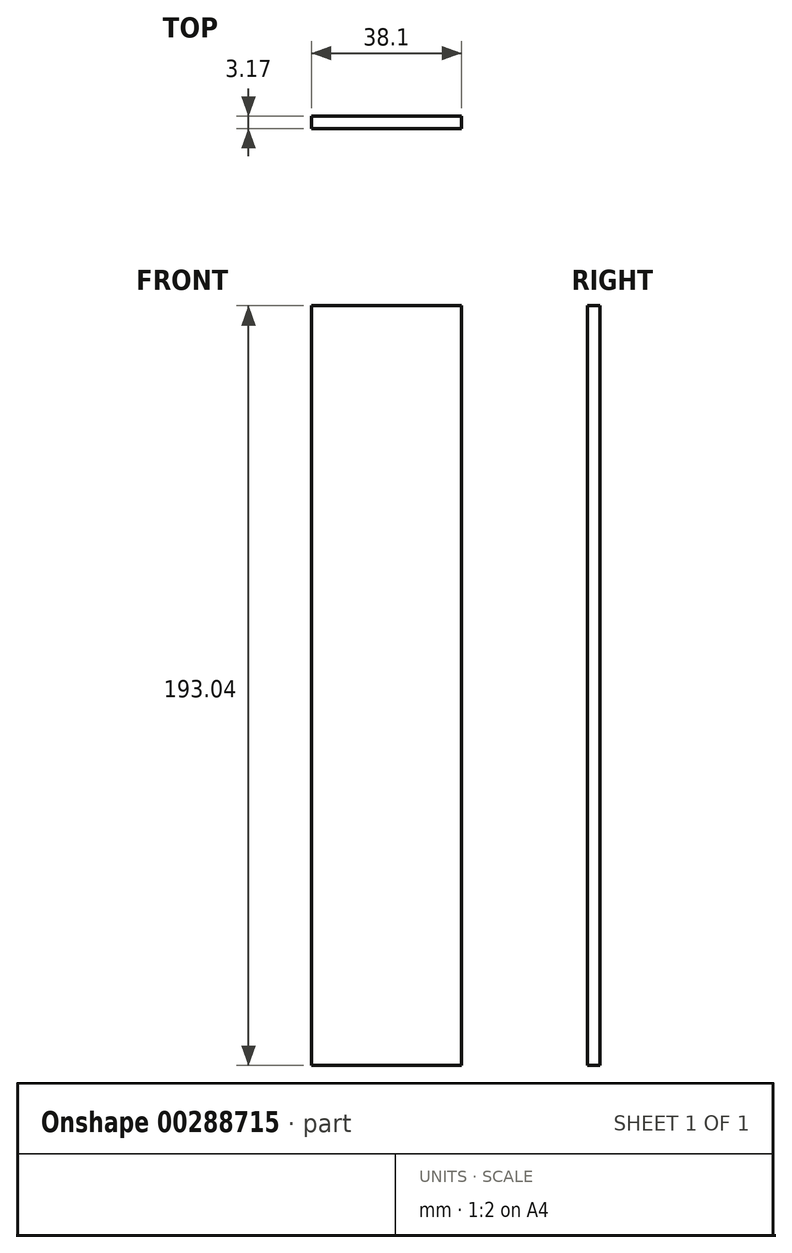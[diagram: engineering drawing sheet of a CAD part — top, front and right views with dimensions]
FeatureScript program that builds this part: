
annotation { "Feature Type Name" : "Feature", "Feature Type Description" : "" }
export const myFeature = defineFeature(function(context is Context, id is Id, definition is map)
    precondition{}
    {
        {
            var Q0;
            Q0=qCreatedBy(makeId("Front.planeOp"),FACE);
            var sketch = newSketch(context, id + "F0", { "sketchPlane" : qUnion([Q0])});
            skLineSegment(sketch, "E0.bottom", {"start": v(19.05, -96.52) * mm, "end": v(-19.05, -96.52) * mm});
            skLineSegment(sketch, "E0.top", {"start": v(19.05, 96.52) * mm, "end": v(-19.05, 96.52) * mm});
            skLineSegment(sketch, "E0.left", {"start": v(19.05, -96.52) * mm, "end": v(19.05, 96.52) * mm});
            skLineSegment(sketch, "E0.right", {"start": v(-19.05, -96.52) * mm, "end": v(-19.05, 96.52) * mm});
            skPoint(sketch, "E0.middle", {"position": v(0, 0) * mm});
            skSolve(sketch);
        }
        {
            var Q0;
            Q0=makeQuery(id+"F0.imprint","IMPRINT",FACE,{"disambiguationData":[TD([[makeQuery(id+"F0.imprint","IMPRINT",EDGE,{"derivedFrom":sQuery(id+"F0.wireOp",EDGE,"E0.bottom")}),-1.0]])]});
            extrude(context, id + "F1", {"entities" : qUnion([Q0]), "depth" : 3.17 * mm});
        }
    });
